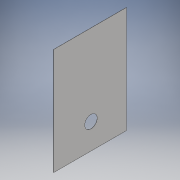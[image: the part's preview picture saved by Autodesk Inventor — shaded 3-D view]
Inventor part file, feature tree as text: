
AUTODESK INVENTOR PART (.ipt)
format: ipt  version: 2018 (Build 220112000, 112)  size: 109,568 bytes
history: native  units: mm
features: extrude x3, sketch x3, projected_geometry x1
ambient origin geometry x8: Origin, YZ Plane, XZ Plane, XY Plane, X Axis, Y Axis, Z Axis, Center Point
bodies: Solid1 (feature_tree)
feature tree (7):
  extrude  "Extrusion1"  Depth=1.6mm
  extrude  "Extrusion2"  Depth=1100.0mm TaperAngle=0.0deg
  extrude  "Extrusion3"  [1 undecoded]
  sketch  "Sketch1"  dims[d0=700.0mm d1=1.6mm]
  sketch  "Sketch2"  dims[d2=1100.0mm d3=0.0mm d4=50.0mm d5=0.0mm]
  projected_geometry  "Projected Loop1"
  sketch  "Sketch3"  dims[d14=50.0mm d15=0.0mm]
note: 1 required parameter value undecoded (feature->parameter linkage not recoverable at this tier; creation-order binding heuristic only, values carry confidence <= 0.55)
